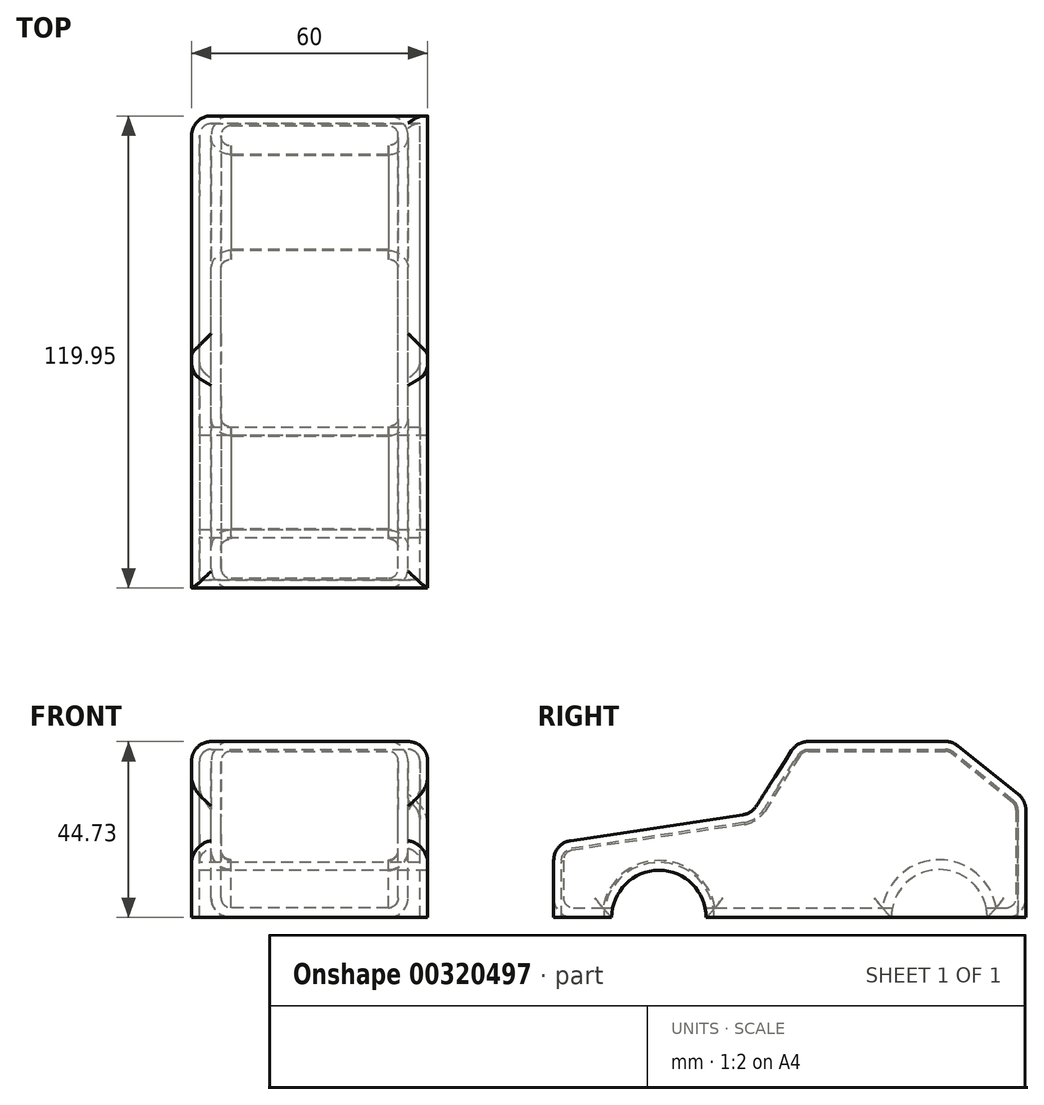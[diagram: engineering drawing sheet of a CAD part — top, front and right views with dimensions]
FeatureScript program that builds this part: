
annotation { "Feature Type Name" : "Feature", "Feature Type Description" : "" }
export const myFeature = defineFeature(function(context is Context, id is Id, definition is map)
    precondition{}
    {
        {
            var Q0;
            Q0=qCreatedBy(makeId("Top.planeOp"),FACE);
            cPlane(context, id + "F0", {"entities" : qUnion([Q0]), "cplaneType" : CPlaneType.OFFSET, "offset" : 3 * mm, "width" : 150 * mm, "height" : 150 * mm});
        }
        {
            var Q0;
            Q0=qCreatedBy(makeId("Right.planeOp"),FACE);
            var sketch = newSketch(context, id + "F1", { "sketchPlane" : qUnion([Q0])});
            skLineSegment(sketch, "E0.bottom", {"start": v(-64.63, 3.8) * mm, "end": v(55.32, 3.8) * mm});
            skLineSegment(sketch, "E0.top", {"start": v(-64.63, 48.53) * mm, "end": v(55.32, 48.53) * mm});
            skLineSegment(sketch, "E0.left", {"start": v(-64.63, 3.8) * mm, "end": v(-64.63, 48.53) * mm});
            skLineSegment(sketch, "E0.right", {"start": v(55.32, 3.8) * mm, "end": v(55.32, 48.53) * mm});
            skCircle(sketch, "E1", {"center": v(-37.9, 3.8) * mm, "radius": 12 * mm});
            skCircle(sketch, "E2", {"center": v(33.32, 3.8) * mm, "radius": 12.19 * mm});
            skLineSegment(sketch, "E3", {"start": v(-64.63, 22.7) * mm, "end": v(-14.35, 30.26) * mm});
            skLineSegment(sketch, "E4", {"start": v(-14.35, 30.26) * mm, "end": v(-2.72, 48.53) * mm});
            skLineSegment(sketch, "E5", {"start": v(36.66, 48.53) * mm, "end": v(55.32, 33.56) * mm});
            skSolve(sketch);
        }
        {
            var Q0;
            {var subQ0=sQuery(id+"F1.wireOp",EDGE,"E3");Q0=makeQuery(id+"F1.imprint","IMPRINT",FACE,{"disambiguationData":[TD([[makeQuery(id+"F1.imprint","IMPRINT",EDGE,{"derivedFrom":subQ0}),-1.0]])]});}
            extrude(context, id + "F2", {"entities" : qUnion([Q0]), "depth" : 25 * mm});
        }
        {
            var Q0;
            Q0=makeQuery(id+"F2.opExtrude","CAP_FACE",FACE,{"disambiguationData":[OSD([sQuery(id+"F1.wireOp",EDGE,"E0.bottom"),sQuery(id+"F1.wireOp",EDGE,"E0.top"),sQuery(id+"F1.wireOp",EDGE,"E0.left"),sQuery(id+"F1.wireOp",EDGE,"E0.right"),sQuery(id+"F1.wireOp",EDGE,"E1"),sQuery(id+"F1.wireOp",EDGE,"E2"),sQuery(id+"F1.wireOp",EDGE,"E3"),sQuery(id+"F1.wireOp",EDGE,"E4"),sQuery(id+"F1.wireOp",EDGE,"E5")])],"isStart":true});
            extrude(context, id + "F3", {"entities" : qUnion([Q0]), "operationType" : NewBodyOperationType.ADD, "depth" : 25 * mm});
        }
        {
            var Q0;
            Q0=makeQuery(id+"F3.opExtrude","CAP_EDGE",EDGE,{"disambiguationData":[OSD([sQuery(id+"F1.wireOp",EDGE,"E4")])],"isStart":false});
            var Q1;
            {var subQ0=sQuery(id+"F1.wireOp",EDGE,"E4");var subQ1=sQuery(id+"F1.wireOp",EDGE,"E0.top");Q1=makeQuery(id+"F3.boolean.opBoolean","MERGE",EDGE,{"derivedFrom":[makeQuery(id+"F2.opExtrude","SWEPT_EDGE",EDGE,{"disambiguationData":[OSD([subQ1,subQ0])]}),makeQuery(id+"F3.opExtrude","SWEPT_EDGE",EDGE,{"disambiguationData":[OSD([subQ1,subQ0])]})]});}
            var Q2;
            {var subQ0=sQuery(id+"F1.wireOp",EDGE,"E4");Q2=makeQuery(id+"F3.boolean.opBoolean","MERGE",FACE,{"derivedFrom":[makeQuery(id+"F2.opExtrude","SWEPT_FACE",FACE,{"disambiguationData":[OSD([subQ0])]}),makeQuery(id+"F3.opExtrude","SWEPT_FACE",FACE,{"disambiguationData":[OSD([subQ0])]})]});}
            var Q3;
            {var subQ0=sQuery(id+"F1.wireOp",EDGE,"E3");var subQ1=sQuery(id+"F1.wireOp",EDGE,"E0.left");Q3=makeQuery(id+"F3.boolean.opBoolean","MERGE",EDGE,{"derivedFrom":[makeQuery(id+"F2.opExtrude","SWEPT_EDGE",EDGE,{"disambiguationData":[OSD([subQ1,subQ0])]}),makeQuery(id+"F3.opExtrude","SWEPT_EDGE",EDGE,{"disambiguationData":[OSD([subQ1,subQ0])]})]});}
            var Q4;
            Q4=makeQuery(id+"F2.opExtrude","CAP_EDGE",EDGE,{"disambiguationData":[OSD([sQuery(id+"F1.wireOp",EDGE,"E0.left")])],"isStart":false});
            var Q5;
            Q5=makeQuery(id+"F3.opExtrude","CAP_EDGE",EDGE,{"disambiguationData":[OSD([sQuery(id+"F1.wireOp",EDGE,"E0.left")])],"isStart":false});
            var Q6;
            {var subQ0=sQuery(id+"F1.wireOp",EDGE,"E0.left");var subQ1=sQuery(id+"F1.wireOp",EDGE,"E0.bottom");Q6=makeQuery(id+"F3.boolean.opBoolean","MERGE",EDGE,{"derivedFrom":[makeQuery(id+"F2.opExtrude","SWEPT_EDGE",EDGE,{"disambiguationData":[OSD([subQ1,subQ0])]}),makeQuery(id+"F3.opExtrude","SWEPT_EDGE",EDGE,{"disambiguationData":[OSD([subQ1,subQ0])]})]});}
            var Q7;
            {var subQ0=sQuery(id+"F1.wireOp",EDGE,"E0.bottom");Q7=makeQuery(id+"F2.opExtrude","CAP_EDGE",EDGE,{"disambiguationData":[OSD([subQ0]),TDD([makeQuery(id+"F1.imprint","IMPRINT",EDGE,{"disambiguationData":[TD([[makeQuery(id+"F1.imprint","INTERSECT",VERTEX,{"disambiguationData":[OD(1.0)],"derivedFrom":[subQ0,sQuery(id+"F1.wireOp",EDGE,"E1")]}),-1.0]])],"derivedFrom":subQ0})])],"isStart":false});}
            var Q8;
            Q8=makeQuery(id+"F2.opExtrude","CAP_FACE",FACE,{"disambiguationData":[OSD([sQuery(id+"F1.wireOp",EDGE,"E0.bottom"),sQuery(id+"F1.wireOp",EDGE,"E0.top"),sQuery(id+"F1.wireOp",EDGE,"E0.left"),sQuery(id+"F1.wireOp",EDGE,"E0.right"),sQuery(id+"F1.wireOp",EDGE,"E1"),sQuery(id+"F1.wireOp",EDGE,"E2"),sQuery(id+"F1.wireOp",EDGE,"E3"),sQuery(id+"F1.wireOp",EDGE,"E4"),sQuery(id+"F1.wireOp",EDGE,"E5")])],"isStart":false});
            var Q9;
            {var subQ0=sQuery(id+"F1.wireOp",EDGE,"E0.right");Q9=makeQuery(id+"F3.boolean.opBoolean","MERGE",FACE,{"derivedFrom":[makeQuery(id+"F2.opExtrude","SWEPT_FACE",FACE,{"disambiguationData":[OSD([subQ0])]}),makeQuery(id+"F3.opExtrude","SWEPT_FACE",FACE,{"disambiguationData":[OSD([subQ0])]})]});}
            var Q10;
            {var subQ0=sQuery(id+"F1.wireOp",EDGE,"E5");Q10=makeQuery(id+"F3.boolean.opBoolean","MERGE",FACE,{"derivedFrom":[makeQuery(id+"F2.opExtrude","SWEPT_FACE",FACE,{"disambiguationData":[OSD([subQ0])]}),makeQuery(id+"F3.opExtrude","SWEPT_FACE",FACE,{"disambiguationData":[OSD([subQ0])]})]});}
            var Q11;
            Q11=makeQuery(id+"F3.opExtrude","CAP_FACE",FACE,{"disambiguationData":[OSD([sQuery(id+"F1.wireOp",EDGE,"E0.bottom"),sQuery(id+"F1.wireOp",EDGE,"E0.top"),sQuery(id+"F1.wireOp",EDGE,"E0.left"),sQuery(id+"F1.wireOp",EDGE,"E0.right"),sQuery(id+"F1.wireOp",EDGE,"E1"),sQuery(id+"F1.wireOp",EDGE,"E2"),sQuery(id+"F1.wireOp",EDGE,"E3"),sQuery(id+"F1.wireOp",EDGE,"E4"),sQuery(id+"F1.wireOp",EDGE,"E5")])],"isStart":false});
            fillet(context, id + "F4", {"entities" : qUnion([Q0, Q1, Q2, Q3, Q4, Q5, Q6, Q7, Q8, Q9, Q10, Q11]), "radius" : 5 * mm, "tangentPropagation" : true, "allowEdgeOverflow" : false});
        }
        {
            var Q0;
            {var subQ0=sQuery(id+"F1.wireOp",EDGE,"E0.bottom");var subQ1=makeQuery(id+"F1.imprint","IMPRINT",EDGE,{"disambiguationData":[TD([[makeQuery(id+"F1.imprint","INTERSECT",VERTEX,{"disambiguationData":[OD(1.0)],"derivedFrom":[subQ0,sQuery(id+"F1.wireOp",EDGE,"E1")]}),-1.0]])],"derivedFrom":subQ0});Q0=makeQuery(id+"F3.boolean.opBoolean","MERGE",FACE,{"derivedFrom":[makeQuery(id+"F2.opExtrude","SWEPT_FACE",FACE,{"disambiguationData":[OSD([subQ0]),TDD([subQ1])]}),makeQuery(id+"F3.opExtrude","SWEPT_FACE",FACE,{"disambiguationData":[OSD([subQ0]),TDD([makeQuery(id+"F2.opExtrude","CAP_EDGE",EDGE,{"disambiguationData":[OSD([subQ0]),TDD([subQ1])],"isStart":true})])]})]});}
            var Q1;
            {var subQ0=sQuery(id+"F1.wireOp",EDGE,"E2");Q1=makeQuery(id+"F3.boolean.opBoolean","MERGE",FACE,{"derivedFrom":[makeQuery(id+"F2.opExtrude","SWEPT_FACE",FACE,{"disambiguationData":[OSD([subQ0])]}),makeQuery(id+"F3.opExtrude","SWEPT_FACE",FACE,{"disambiguationData":[OSD([subQ0])]})]});}
            var Q2;
            {var subQ0=sQuery(id+"F1.wireOp",EDGE,"E1");Q2=makeQuery(id+"F3.boolean.opBoolean","MERGE",FACE,{"derivedFrom":[makeQuery(id+"F2.opExtrude","SWEPT_FACE",FACE,{"disambiguationData":[OSD([subQ0])]}),makeQuery(id+"F3.opExtrude","SWEPT_FACE",FACE,{"disambiguationData":[OSD([subQ0])]})]});}
            shell(context, id + "F5", {"entities" : qUnion([Q0, Q1, Q2]), "thickness" : 2.5 * mm});
        }
        {
            var Q0;
            {var subQ0=sQuery(id+"F1.wireOp",EDGE,"E4");Q0=makeQuery(id+"F3.boolean.opBoolean","MERGE",FACE,{"derivedFrom":[makeQuery(id+"F2.opExtrude","SWEPT_FACE",FACE,{"disambiguationData":[OSD([subQ0])]}),makeQuery(id+"F3.opExtrude","SWEPT_FACE",FACE,{"disambiguationData":[OSD([subQ0])]})]});}
            extrude(context, id + "F6", {"entities" : qUnion([Q0]), "operationType" : NewBodyOperationType.REMOVE, "oppositeDirection" : true, "depth" : 1 * mm});
        }
        {
            var Q0;
            Q0=makeQuery(id+"F6.boolean.opBoolean","COPY",FACE,{"derivedFrom":makeQuery(id+"F6.opExtrude","CAP_FACE",FACE,{"disambiguationData":[OSD([sQuery(id+"F1.wireOp",EDGE,"E4")])],"isStart":false})});
            extrude(context, id + "F7", {"entities" : qUnion([Q0]), "operationType" : NewBodyOperationType.ADD, "depth" : 1 * mm});
        }
        {
            var Q0;
            {var subQ0=sQuery(id+"F1.wireOp",EDGE,"E3");Q0=makeQuery(id+"F1.imprint","IMPRINT",FACE,{"disambiguationData":[TD([[makeQuery(id+"F1.imprint","IMPRINT",EDGE,{"derivedFrom":subQ0}),-1.0]])]});}
            var Q1;
            {var subQ0=sQuery(id+"F1.wireOp",EDGE,"E1");var subQ1=sQuery(id+"F1.wireOp",EDGE,"E0.bottom");var subQ2=makeQuery(id+"F1.imprint","INTERSECT",VERTEX,{"disambiguationData":[OD(0.0)],"derivedFrom":[subQ1,subQ0]});Q1=makeQuery(id+"F1.imprint","IMPRINT",FACE,{"disambiguationData":[TD([[makeQuery(id+"F1.imprint","IMPRINT",EDGE,{"disambiguationData":[TD([[subQ2,-1.0]])],"derivedFrom":subQ1}),1.0]])]});}
            var Q2;
            {var subQ0=sQuery(id+"F1.wireOp",EDGE,"E2");var subQ1=sQuery(id+"F1.wireOp",EDGE,"E0.bottom");var subQ2=makeQuery(id+"F1.imprint","INTERSECT",VERTEX,{"disambiguationData":[OD(0.0)],"derivedFrom":[subQ1,subQ0]});Q2=makeQuery(id+"F1.imprint","IMPRINT",FACE,{"disambiguationData":[TD([[makeQuery(id+"F1.imprint","IMPRINT",EDGE,{"disambiguationData":[TD([[subQ2,-1.0]])],"derivedFrom":subQ1}),1.0]])]});}
            extrude(context, id + "F8", {"entities" : qUnion([Q0, Q1, Q2]), "endBound" : BoundingType.SYMMETRIC, "depth" : 60 * mm});
        }
        {
            var Q0;
            {var subQ0=sQuery(id+"F1.wireOp",EDGE,"E0.bottom");var subQ2=sQuery(id+"FITDKB5VjfbWcqy_1.wireOp",EDGE,"67bb000e-cad4-407a-b79c-1ce1cb6a6c2a");Q0=makeQuery(id+"F9.boolean.opBoolean","COPY",EDGE,{"disambiguationData":[TD([makeQuery(id+"F8.opExtrude","SWEPT_FACE",FACE,{"disambiguationData":[OSD([subQ0])]})])],"derivedFrom":makeQuery(id+"F9.opExtrude","CAP_EDGE",EDGE,{"disambiguationData":[OSD([subQ2])],"isStart":true})});}
            var Q1;
            Q1=makeQuery(id+"F8.opExtrude","SWEPT_EDGE",EDGE,{"disambiguationData":[OSD([sQuery(id+"F1.wireOp",EDGE,"E0.left"),sQuery(id+"F1.wireOp",EDGE,"E3")])]});
            var Q2;
            {var subQ0=sQuery(id+"F1.wireOp",EDGE,"E0.bottom");var subQ1=sQuery(id+"FITDKB5VjfbWcqy_1.wireOp",EDGE,"412f1874-058b-4a8f-9d57-cb0ba7ac9deb0.MirrorCS");Q2=makeQuery(id+"F9.boolean.opBoolean","COPY",EDGE,{"disambiguationData":[TD([makeQuery(id+"F8.opExtrude","SWEPT_FACE",FACE,{"disambiguationData":[OSD([subQ0])]})])],"derivedFrom":makeQuery(id+"F9.opExtrude","CAP_EDGE",EDGE,{"disambiguationData":[OSD([subQ1])],"isStart":true})});}
            var Q3;
            Q3=makeQuery(id+"F8.opExtrude","SWEPT_FACE",FACE,{"disambiguationData":[OSD([sQuery(id+"F1.wireOp",EDGE,"E3")])]});
            var Q4;
            Q4=makeQuery(id+"F8.opExtrude","SWEPT_FACE",FACE,{"disambiguationData":[OSD([sQuery(id+"F1.wireOp",EDGE,"E0.top")])]});
            var Q5;
            Q5=makeQuery(id+"F9.boolean.opBoolean","INTERSECT",EDGE,{"derivedFrom":[makeQuery(id+"F8.opExtrude","SWEPT_FACE",FACE,{"disambiguationData":[OSD([sQuery(id+"F1.wireOp",EDGE,"E5")])]}),makeQuery(id+"F9.opExtrude","SWEPT_FACE",FACE,{"disambiguationData":[OSD([sQuery(id+"FITDKB5VjfbWcqy_1.wireOp",EDGE,"412f1874-058b-4a8f-9d57-cb0ba7ac9deb0.MirrorCS")])]})]});
            var Q6;
            Q6=makeQuery(id+"F9.boolean.opBoolean","INTERSECT",EDGE,{"disambiguationData":[OD(1.0)],"derivedFrom":[makeQuery(id+"F8.opExtrude","SWEPT_FACE",FACE,{"disambiguationData":[OSD([sQuery(id+"F1.wireOp",EDGE,"E0.right")])]}),makeQuery(id+"F9.opExtrude","SWEPT_FACE",FACE,{"disambiguationData":[OSD([sQuery(id+"FITDKB5VjfbWcqy_1.wireOp",EDGE,"412f1874-058b-4a8f-9d57-cb0ba7ac9deb0.MirrorCS")])]})]});
            var Q7;
            Q7=makeQuery(id+"F8.opExtrude","SWEPT_FACE",FACE,{"disambiguationData":[OSD([sQuery(id+"F1.wireOp",EDGE,"E5")])]});
            var Q8;
            Q8=makeQuery(id+"F8.opExtrude","CAP_EDGE",EDGE,{"disambiguationData":[OSD([sQuery(id+"F1.wireOp",EDGE,"E0.right")])],"isStart":true});
            fillet(context, id + "F10", {"entities" : qUnion([Q0, Q1, Q2, Q3, Q4, Q5, Q6, Q7, Q8]), "radius" : 5 * mm, "tangentPropagation" : true, "allowEdgeOverflow" : false});
        }
        {
            var Q0;
            Q0=makeQuery(id+"F8.opExtrude","SWEPT_FACE",FACE,{"disambiguationData":[OSD([sQuery(id+"F1.wireOp",EDGE,"E0.bottom")])]});
            shell(context, id + "F11", {"entities" : qUnion([Q0]), "thickness" : 2 * mm});
        }
    });
